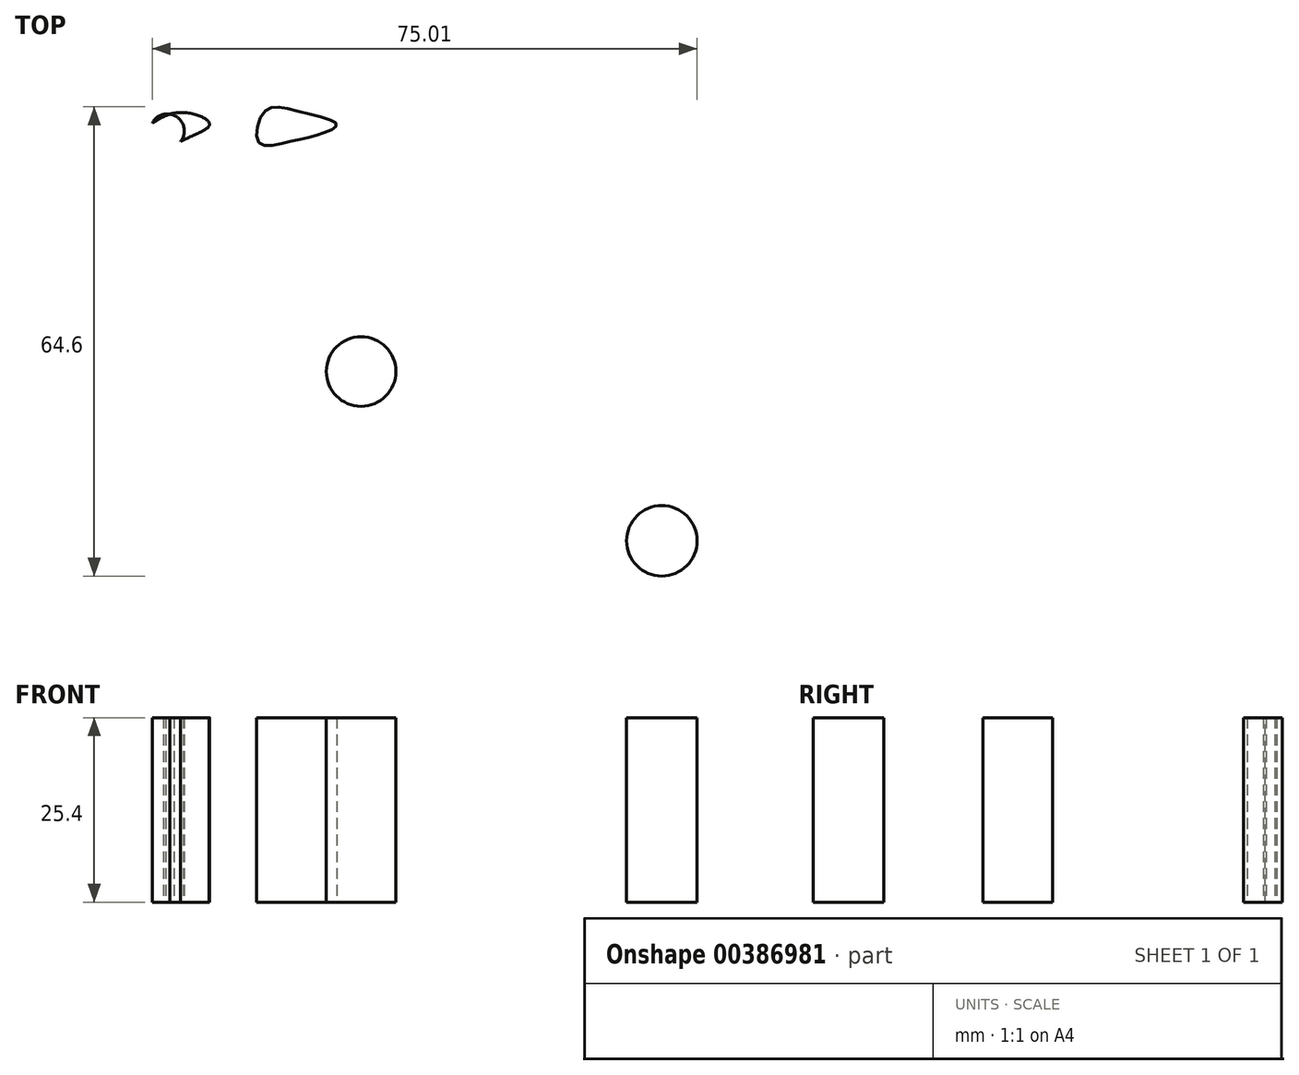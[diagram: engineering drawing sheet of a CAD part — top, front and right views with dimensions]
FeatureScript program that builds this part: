
annotation { "Feature Type Name" : "Feature", "Feature Type Description" : "" }
export const myFeature = defineFeature(function(context is Context, id is Id, definition is map)
    precondition{}
    {
        {
            var Q0;
            Q0=qCreatedBy(makeId("Top.planeOp"),FACE);
            var sketch = newSketch(context, id + "F0", { "sketchPlane" : qUnion([Q0])});
            skFitSpline(sketch, "E0", {"points": [v(-40.9, 39.4) * mm, v(-37.6, 44.22) * mm, v(-33.69, 47.52) * mm, v(-33.39, 47.52) * mm, v(-36.4, 51.74) * mm, v(-37.6, 60.76) * mm, v(-34.9, 70.38) * mm, v(-30.68, 72.8) * mm, v(-31.28, 69.78) * mm, v(-32.49, 58.65) * mm, v(-29.48, 51.74) * mm, v(-24.97, 47.52) * mm, v(-18.95, 47.52) * mm, v(-15.04, 50.53) * mm, v(-12.63, 62.86) * mm, v(-14.74, 70.69) * mm, v(-17.75, 74) * mm, v(-11.43, 73.1) * mm, v(-7.22, 62.56) * mm, v(-7.22, 55.35) * mm, v(-8.42, 49.63) * mm, v(-10.53, 45.42) * mm, v(0, 42.71) * mm, v(36.4, 35.2) * mm, v(67.68, 20.15) * mm, v(77.3, -8.72) * mm, v(77.9, -22.26) * mm, v(86.33, -27.07) * mm, v(101.97, -19.25) * mm, v(107.08, -3.6) * mm, v(105.58, 0) * mm, v(110.7, -4.51) * mm, v(110.09, -14.14) * mm, v(105.28, -23.76) * mm, v(94.45, -30.08) * mm, v(81.21, -30.98) * mm, v(74, -26.47) * mm, v(55.27, -29.78) * mm, v(71.89, -30.08) * mm], "startDerivative": vector(131.92, 223.11) * mm, "endDerivative": vector(-49.6, -21.15) * mm});
            skFitSpline(sketch, "E1", {"points": [v(55.27, -29.78) * mm, v(50.46, -38.2) * mm, v(36.32, -48.13) * mm, v(27.6, -51.44) * mm, v(30, -47.83) * mm, v(25.5, -46.92) * mm, v(29.4, -43.92) * mm, v(38.73, -37.9) * mm, v(47.45, -29.78) * mm, v(41.43, -26.47) * mm, v(21.28, -35.8) * mm, v(6.84, -26.47) * mm, v(2.93, -23.76) * mm, v(0.83, -23.46) * mm, v(4.44, -22.26) * mm, v(8.95, -22.86) * mm, v(5.04, -20.75) * mm, v(11.36, -21.06) * mm, v(20.68, -26.47) * mm, v(20.08, -22.26) * mm, v(18.27, -11.73) * mm, v(20.98, -9.02) * mm, v(15.57, -7.22) * mm, v(0.23, -3.3) * mm, v(-10.9, 0) * mm, v(-23.84, 4.21) * mm, v(-35.87, 4.51) * mm, v(-39.78, 0) * mm, v(-39.78, -6.92) * mm, v(-42.49, -4.21) * mm, v(-44.6, -6.92) * mm, v(-44.9, -3.3) * mm, v(-43.69, 5.41) * mm, v(-40.38, 9.93) * mm, v(-55.42, 0) * mm, v(-61.74, 0) * mm, v(-47.6, 20.45) * mm, v(-64.86, 18.35) * mm], "startDerivative": vector(-139.2, -323.53) * mm, "endDerivative": vector(-330.46, 89.38) * mm});
            skCircle(sketch, "E2", {"center": v(-23.76, 73.4) * mm, "radius": 5.8 * mm});
            skFitSpline(sketch, "E3", {"points": [v(-40.38, 9.93) * mm, v(-15.94, 14.74) * mm, v(-5.41, 14.74) * mm, v(0, 20.45) * mm, v(0, 23.76) * mm], "startDerivative": vector(24.68, 23.73) * mm, "endDerivative": vector(-3.6, 17.83) * mm});
            skFitSpline(sketch, "E4", {"points": [v(7.52, 23.76) * mm, v(8.42, 19.85) * mm, v(6.92, 15.04) * mm, v(5.72, 6.02) * mm, v(0, -3.25) * mm, v(-10.25, 0.58) * mm], "startDerivative": vector(8.1, -23.42) * mm, "endDerivative": vector(10.24, 1.16) * mm});
            skLineSegment(sketch, "E5", {"start": v(-40.9, 39.4) * mm, "end": v(-56.57, 32.48) * mm});
            skLineSegment(sketch, "E6", {"start": v(-56.57, 32.48) * mm, "end": v(-53.96, 26.58) * mm});
            skLineSegment(sketch, "E7", {"start": v(-53.96, 26.58) * mm, "end": v(-41.84, 27.26) * mm});
            skLineSegment(sketch, "E8", {"start": v(-41.84, 27.26) * mm, "end": v(-46.44, 23.28) * mm});
            skLineSegment(sketch, "E9", {"start": v(-46.44, 23.28) * mm, "end": v(-48.9, 20.82) * mm});
            skFitSpline(sketch, "E10", {"points": [v(-50.12, 20.21) * mm, v(-39.7, 21.44) * mm, v(-32.34, 20.52) * mm, v(-32.03, 20.52) * mm, v(-19.45, 20.21) * mm, v(-28.96, 16.84) * mm, v(-40, 13.46) * mm, v(-48.9, 6.72) * mm, v(-50.43, 2.11) * mm, v(-46.44, 5.49) * mm, v(-46.14, 1.5) * mm, v(-45.22, 1.5) * mm, v(-45.52, 1.5) * mm], "startDerivative": vector(85.53, 17.75) * mm, "endDerivative": vector(-25, -2.98) * mm});
            skFitSpline(sketch, "E11", {"points": [v(37.6, -7.7) * mm, v(32.07, -7.09) * mm, v(27.47, -7.4) * mm, v(20.73, -9.54) * mm], "startDerivative": vector(-17.35, 2.37) * mm, "endDerivative": vector(-19.1, -6.97) * mm});
            skLineSegment(sketch, "E12", {"start": v(105.58, 0) * mm, "end": v(102.31, 0) * mm});
            skLineSegment(sketch, "E13", {"start": v(105.69, 0.27) * mm, "end": v(103.23, 3.34) * mm});
            skLineSegment(sketch, "E14", {"start": v(105.69, 0.89) * mm, "end": v(105.38, 6.4) * mm});
            skLineSegment(sketch, "E15", {"start": v(105.69, 0.27) * mm, "end": v(100.78, 2.73) * mm});
            skFitSpline(sketch, "E16", {"points": [v(37.6, -7.7) * mm, v(43.73, -7.7) * mm, v(53.24, -8.68) * mm, v(56.3, -11.38) * mm, v(56, -11.07) * mm], "startDerivative": vector(18.69, -0.48) * mm, "endDerivative": vector(-5.62, 6.05) * mm});
            skFitSpline(sketch, "E17", {"points": [v(-17, 41.99) * mm, v(-12.7, 41.99) * mm, v(-7.18, 40.15) * mm, v(-9.03, 38.92) * mm, v(-13.93, 37.7) * mm, v(-17.92, 37.7) * mm, v(-17, 41.99) * mm]});
            skFitSpline(sketch, "E18", {"points": [v(-27.43, 41.68) * mm, v(-29.58, 41.68) * mm, v(-32.64, 41.07) * mm, v(-36.63, 38.3) * mm, v(-32.95, 36.77) * mm, v(-30.19, 36.77) * mm, v(-24.67, 40.15) * mm, v(-27.43, 41.68) * mm]});
            skCircle(sketch, "E19", {"center": v(-30.5, 39.23) * mm, "radius": 2.34 * mm});
            skCircle(sketch, "E20", {"center": v(37.6, -17.2) * mm, "radius": 4.85 * mm});
            skCircle(sketch, "E21", {"center": v(-3.81, 6.1) * mm, "radius": 4.8 * mm});
            skFitSpline(sketch, "E22", {"points": [v(-32.95, 32.48) * mm, v(-24.67, 37.7) * mm, v(-20.68, 39.4) * mm, v(-20.99, 41.68) * mm, v(-24.67, 44.22) * mm, v(-32.95, 44.22) * mm, v(-40, 40.93) * mm, v(-36.63, 38.3) * mm, v(-29.58, 41.68) * mm, v(-24.67, 40.15) * mm, v(-30.19, 36.77) * mm, v(-32.95, 32.48) * mm]});
            skLineSegment(sketch, "E23", {"start": v(-45.22, 1.5) * mm, "end": v(-46.44, 5.49) * mm});
            skSolve(sketch);
        }
        {
            var Q0;
            {var subQ0=sQuery(id+"F0.wireOp",EDGE,"E22");var subQ1=sQuery(id+"F0.wireOp",EDGE,"E19");var subQ2=makeQuery(id+"F0.imprint","INTERSECT",VERTEX,{"disambiguationData":[OD(0.0)],"derivedFrom":[subQ1,subQ0]});Q0=makeQuery(id+"F0.imprint","IMPRINT",FACE,{"disambiguationData":[TD([[makeQuery(id+"F0.imprint","IMPRINT",EDGE,{"disambiguationData":[TD([[subQ2,-1.0]])],"derivedFrom":subQ1}),1.0]])]});}
            var Q1;
            Q1=makeQuery(id+"F0.imprint","IMPRINT",FACE,{"disambiguationData":[TD([[makeQuery(id+"F0.imprint","IMPRINT",EDGE,{"derivedFrom":sQuery(id+"F0.wireOp",EDGE,"E17")}),-1.0]])]});
            var Q2;
            Q2=makeQuery(id+"F0.imprint","IMPRINT",FACE,{"disambiguationData":[TD([[makeQuery(id+"F0.imprint","IMPRINT",EDGE,{"derivedFrom":sQuery(id+"F0.wireOp",EDGE,"E21")}),1.0]])]});
            var Q3;
            Q3=makeQuery(id+"F0.imprint","IMPRINT",FACE,{"disambiguationData":[TD([[makeQuery(id+"F0.imprint","IMPRINT",EDGE,{"derivedFrom":sQuery(id+"F0.wireOp",EDGE,"E20")}),1.0]])]});
            var Q4;
            {var subQ0=sQuery(id+"F0.wireOp",EDGE,"E22");var subQ1=sQuery(id+"F0.wireOp",EDGE,"E18");var subQ2=makeQuery(id+"F0.imprint","INTERSECT",VERTEX,{"disambiguationData":[OD(1.0)],"derivedFrom":[subQ1,subQ0]});Q4=makeQuery(id+"F0.imprint","IMPRINT",FACE,{"disambiguationData":[TD([[makeQuery(id+"F0.imprint","IMPRINT",EDGE,{"disambiguationData":[TD([[subQ2,-1.0]])],"derivedFrom":subQ1}),1.0]])]});}
            extrude(context, id + "F1", {"entities" : qUnion([Q0, Q1, Q2, Q3, Q4]), "depth" : 25.4 * mm});
        }
    });
